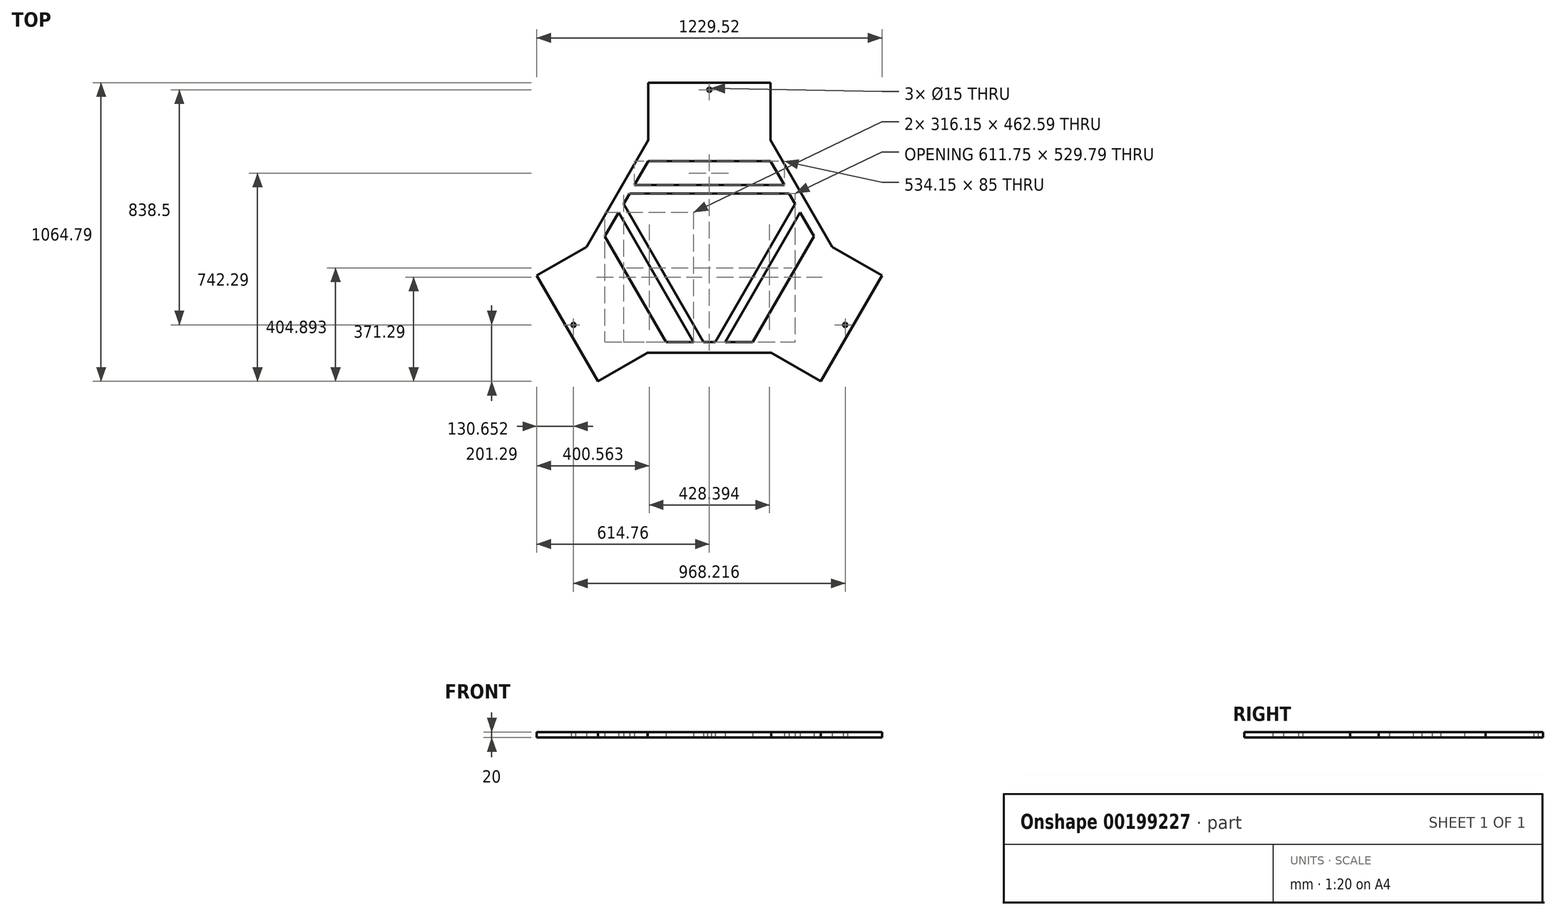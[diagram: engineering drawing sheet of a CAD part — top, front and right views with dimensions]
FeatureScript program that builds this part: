
annotation { "Feature Type Name" : "Feature", "Feature Type Description" : "" }
export const myFeature = defineFeature(function(context is Context, id is Id, definition is map)
    precondition{}
    {
        {
            var Q0;
            Q0=qCreatedBy(makeId("Top.planeOp"),FACE);
            var sketch = newSketch(context, id + "F0", { "sketchPlane" : qUnion([Q0])});
            skPoint(sketch, "E0.middle", {"position": v(0, 0) * mm});
            skLineSegment(sketch, "E1", {"start": v(-263.27, -152) * mm, "end": v(263.27, -152) * mm, "construction": true});
            skLineSegment(sketch, "E2", {"start": v(0, 304) * mm, "end": v(-263.27, -152) * mm, "construction": true});
            skLineSegment(sketch, "E3", {"start": v(0, 304) * mm, "end": v(263.27, -152) * mm, "construction": true});
            skLineSegment(sketch, "E4", {"start": v(263.27, -152) * mm, "end": v(-131.64, 76) * mm, "construction": true});
            skLineSegment(sketch, "E5", {"start": v(0, 304) * mm, "end": v(0, -152) * mm, "construction": true});
            skLineSegment(sketch, "E6", {"start": v(-263.27, -152) * mm, "end": v(131.64, 76) * mm, "construction": true});
            skLineSegment(sketch, "E7.bottom", {"start": v(218, 584) * mm, "end": v(-218, 584) * mm});
            skLineSegment(sketch, "E7.top", {"start": v(218, 304) * mm, "end": v(-218, 304) * mm});
            skPoint(sketch, "E7.middle", {"position": v(0, 444) * mm});
            skLineSegment(sketch, "E8.MirrorCS", {"start": v(614.76, -103.2) * mm, "end": v(396.76, -480.8) * mm});
            skLineSegment(sketch, "E9.MirrorCS", {"start": v(372.27, 36.8) * mm, "end": v(154.27, -340.8) * mm, "construction": true});
            skLineSegment(sketch, "E10.MirrorCS", {"start": v(-154.27, -340.8) * mm, "end": v(-372.27, 36.8) * mm, "construction": true});
            skLineSegment(sketch, "E11.MirrorCS", {"start": v(-614.76, -103.2) * mm, "end": v(-372.27, 36.8) * mm, "construction": true});
            skLineSegment(sketch, "E12.MirrorCS", {"start": v(-396.76, -480.8) * mm, "end": v(-614.76, -103.2) * mm});
            skLineSegment(sketch, "E13.MirrorCS", {"start": v(-396.76, -480.8) * mm, "end": v(-154.27, -340.8) * mm, "construction": true});
            skLineSegment(sketch, "E14", {"start": v(-720.91, 846.68) * mm, "end": v(759.09, -433.32) * mm, "construction": true});
            skLineSegment(sketch, "E15", {"start": v(759.09, 846.68) * mm, "end": v(-720.91, -433.32) * mm, "construction": true});
            skPoint(sketch, "E16.cornerSnap0", {"position": v(65.82, -38) * mm});
            skLineSegment(sketch, "E17", {"start": v(-218, 584) * mm, "end": v(-218, 380) * mm});
            skLineSegment(sketch, "E18", {"start": v(-218, 380) * mm, "end": v(-328.04, 189.4) * mm});
            skLineSegment(sketch, "E19", {"start": v(-131.64, 76) * mm, "end": v(-476.1, 274.88) * mm, "construction": true});
            skLineSegment(sketch, "E20.MirrorCS", {"start": v(-438.09, -1.2) * mm, "end": v(-328.04, 189.4) * mm});
            skLineSegment(sketch, "E21", {"start": v(-218, 380) * mm, "end": v(218, 380) * mm, "construction": true});
            skLineSegment(sketch, "E22", {"start": v(-218, 380) * mm, "end": v(-218, 304) * mm, "construction": true});
            skLineSegment(sketch, "E23", {"start": v(218, 380) * mm, "end": v(218, 304) * mm, "construction": true});
            skLineSegment(sketch, "E24.MirrorCS", {"start": v(218, 584) * mm, "end": v(218, 380) * mm});
            skLineSegment(sketch, "E25.MirrorCS", {"start": v(218, 380) * mm, "end": v(328.04, 189.4) * mm});
            skLineSegment(sketch, "E26.MirrorCS", {"start": v(438.09, -1.2) * mm, "end": v(328.04, 189.4) * mm});
            skLineSegment(sketch, "E27.MirrorCS", {"start": v(-614.76, -103.2) * mm, "end": v(-438.09, -1.2) * mm});
            skLineSegment(sketch, "E28.MirrorCS", {"start": v(-396.76, -480.8) * mm, "end": v(-220.09, -378.8) * mm});
            skLineSegment(sketch, "E29.MirrorCS", {"start": v(-220.09, -378.8) * mm, "end": v(0, -378.8) * mm});
            skLineSegment(sketch, "E30.MirrorCS", {"start": v(220.09, -378.8) * mm, "end": v(0, -378.8) * mm});
            skLineSegment(sketch, "E31.MirrorCS", {"start": v(396.76, -480.8) * mm, "end": v(220.09, -378.8) * mm});
            skLineSegment(sketch, "E32.MirrorCS", {"start": v(614.76, -103.2) * mm, "end": v(438.09, -1.2) * mm});
            skCircle(sketch, "E33", {"center": v(0, 0) * mm, "radius": 559 * mm, "construction": true});
            skCircle(sketch, "E34", {"center": v(0, 559) * mm, "radius": 7.5 * mm});
            skCircle(sketch, "E35.MirrorC", {"center": v(-484.1, -279.5) * mm, "radius": 7.5 * mm});
            skCircle(sketch, "E36.MirrorC", {"center": v(484.1, -279.5) * mm, "radius": 7.5 * mm});
            skLineSegment(sketch, "E37", {"start": v(-267.07, 219) * mm, "end": v(267.07, 219) * mm});
            skLineSegment(sketch, "E38", {"start": v(-218, 304) * mm, "end": v(-267.07, 219) * mm});
            skLineSegment(sketch, "E39.MirrorCS", {"start": v(218, 304) * mm, "end": v(267.07, 219) * mm});
            skLineSegment(sketch, "E40", {"start": v(-284.4, 189) * mm, "end": v(-295.14, 170.4) * mm});
            skLineSegment(sketch, "E41", {"start": v(-284.4, 189) * mm, "end": v(0, 189) * mm});
            skLineSegment(sketch, "E42.MirrorCS", {"start": v(284.4, 189) * mm, "end": v(0, 189) * mm});
            skLineSegment(sketch, "E43.MirrorCS", {"start": v(284.4, 189) * mm, "end": v(295.14, 170.4) * mm});
            skLineSegment(sketch, "E44.MirrorCS", {"start": v(-305.88, 151.8) * mm, "end": v(-163.68, -94.5) * mm});
            skLineSegment(sketch, "E45.MirrorCS", {"start": v(-21.48, -340.8) * mm, "end": v(-163.68, -94.5) * mm});
            skLineSegment(sketch, "E46.MirrorCS", {"start": v(305.88, 151.8) * mm, "end": v(163.68, -94.5) * mm});
            skLineSegment(sketch, "E47.MirrorCS", {"start": v(21.48, -340.8) * mm, "end": v(163.68, -94.5) * mm});
            skLineSegment(sketch, "E48.MirrorCS", {"start": v(305.88, 151.8) * mm, "end": v(295.14, 170.4) * mm});
            skLineSegment(sketch, "E49.MirrorCS", {"start": v(21.48, -340.8) * mm, "end": v(0, -340.8) * mm});
            skLineSegment(sketch, "E50.MirrorCS", {"start": v(-305.88, 151.8) * mm, "end": v(-295.14, 170.4) * mm});
            skLineSegment(sketch, "E51.MirrorCS", {"start": v(-21.48, -340.8) * mm, "end": v(0, -340.8) * mm});
            skLineSegment(sketch, "E52.MirrorCS", {"start": v(-323.2, 121.8) * mm, "end": v(-56.12, -340.8) * mm});
            skLineSegment(sketch, "E53.MirrorCS", {"start": v(-154.27, -340.8) * mm, "end": v(-372.27, 36.8) * mm});
            skLineSegment(sketch, "E54.MirrorCS", {"start": v(-372.27, 36.8) * mm, "end": v(-323.2, 121.8) * mm});
            skLineSegment(sketch, "E55.MirrorCS", {"start": v(-154.27, -340.8) * mm, "end": v(-56.12, -340.8) * mm});
            skLineSegment(sketch, "E56.MirrorCS", {"start": v(56.12, -340.8) * mm, "end": v(323.2, 121.8) * mm});
            skLineSegment(sketch, "E57.MirrorCS", {"start": v(372.27, 36.8) * mm, "end": v(154.27, -340.8) * mm});
            skLineSegment(sketch, "E58.MirrorCS", {"start": v(372.27, 36.8) * mm, "end": v(323.2, 121.8) * mm});
            skLineSegment(sketch, "E59.MirrorCS", {"start": v(154.27, -340.8) * mm, "end": v(56.12, -340.8) * mm});
            skLineSegment(sketch, "E60", {"start": v(-267.07, 219) * mm, "end": v(-295.14, 170.4) * mm, "construction": true});
            skSolve(sketch);
        }
        {
            var Q0;
            Q0=qSketchRegion(id+"F0",true);
            extrude(context, id + "F1", {"entities" : qUnion([Q0]), "depth" : 20 * mm});
        }
    });
